# Revit family: 307_9ea7d12cee1e489fa1276d4329909b
name_source: partatom
category: Pipe Accessories
units: mm (PartAtom-declared; Revit-internal decimal feet)

## family parameters
Always vertical = Yes
Cut with Voids When Loaded = No
Part Type = Breaks Into
Round Connector Dimension = Use Diameter
Shared = No
Work Plane-Based = No

## types (4) — shared parameters
B1 = 2 mm  [stored 0.00656168 ft]
B11 = 13 mm  [stored 0.0426509 ft]
B11__ve = -13 mm  [stored -0.0426509 ft]
B1__ve = -2 mm  [stored -0.00656168 ft]
CenSd_NR1_6 = 15 mm  [stored 0.0492126 ft]
CenSd_NR_6 = 10 mm  [stored 0.0328084 ft]
Description = Flanged deaerator, swiveling air vent, max. press. 10 bar
EEE = 5 mm  [stored 0.0164042 ft]
HD2 = 5 mm  [stored 0.0164042 ft]
L2D = 511 mm
L2D_Min = 3048 mm
Manufacturer = FAR
NR = 11 mm
NR1 = 18 mm
QmdConnectorList = 301;D;302;D
R2 = 13 mm  [stored 0.0426509 ft]
RH = 12 mm  [stored 0.0393701 ft]
RR = 8 mm  [stored 0.0262467 ft]
W2D = 100 mm  [stored 0.328084 ft]
magiPartTypeId = 307
magiProductFamilyId = 9ea7d12cee1e489fa1276d4329909b

## per-type parameters (varying)
| type | A | D | D12 | DM1 | DM2 | E1 | E2 | E3 | E4 | ER | G | G4 | HC | HCD2 | HE | HE1 | HT | L1 | LL | LM | R | RC | magiProductId |
| 2258 100 | 178 mm  [stored 0.58399 ft] | 100 mm | 75 mm  [stored 0.246063 ft] | 60 mm  [stored 0.19685 ft] | 52 mm  [stored 0.170604 ft] | 16 mm | 39 mm  [stored 0.127953 ft] | 20 mm  [stored 0.0656168 ft] | 20 mm  [stored 0.0656168 ft] | 86 mm | 157 mm | 63 mm | 46 mm | 65 mm  [stored 0.213255 ft] | Yes | No | 390 mm | 26 mm | 256 mm | 430 mm | 50 mm  [stored 0.164042 ft] | 39 mm  [stored 0.127953 ft] | 25a53c9746d945658aea968eb50474 |
| 2258 50 | 148 mm | 50 mm | 50 mm  [stored 0.164042 ft] | 30 mm  [stored 0.0984252 ft] | 32 mm  [stored 0.104987 ft] | 13 mm  [stored 0.0426509 ft] | 32 mm  [stored 0.104987 ft] | 16 mm | 16 mm | 70 mm  [stored 0.229659 ft] | 104 mm | 42 mm  [stored 0.137795 ft] | 28 mm | 40 mm  [stored 0.131234 ft] | No | Yes | 317 mm | 17 mm | 172 mm  [stored 0.564304 ft] | 280 mm | 25 mm  [stored 0.082021 ft] | 32 mm  [stored 0.104987 ft] | 26d32bb700464772a070e503b4e49b |
| 2258 65 | 148 mm | 65 mm | 50 mm  [stored 0.164042 ft] | 39 mm  [stored 0.127953 ft] | 32 mm  [stored 0.104987 ft] | 13 mm  [stored 0.0426509 ft] | 32 mm  [stored 0.104987 ft] | 16 mm | 16 mm | 70 mm  [stored 0.229659 ft] | 104 mm | 42 mm  [stored 0.137795 ft] | 28 mm | 40 mm  [stored 0.131234 ft] | Yes | No | 317 mm | 17 mm | 172 mm  [stored 0.564304 ft] | 280 mm | 33 mm | 32 mm  [stored 0.104987 ft] | 66933bce9db34afe94ccd17522d7ed |
| 2258 80 | 178 mm  [stored 0.58399 ft] | 80 mm | 75 mm  [stored 0.246063 ft] | 48 mm  [stored 0.15748 ft] | 48 mm  [stored 0.15748 ft] | 16 mm | 39 mm  [stored 0.127953 ft] | 20 mm  [stored 0.0656168 ft] | 20 mm  [stored 0.0656168 ft] | 86 mm | 157 mm | 63 mm | 42 mm  [stored 0.137795 ft] | 60 mm  [stored 0.19685 ft] | Yes | No | 390 mm | 26 mm | 256 mm | 430 mm | 40 mm  [stored 0.131234 ft] | 39 mm  [stored 0.127953 ft] | 75b5f049f10b4ad7af4111e15f281b |

note: column(s) folded — value = type name in every type: MC Product Code

note: [stored X ft] marks values corroborated as IEEE doubles in the binary element streams (Revit-internal decimal feet)

## geometry (parser evidence)
native form markers: Sweep x3
no freeform markers — native parametric forms only
